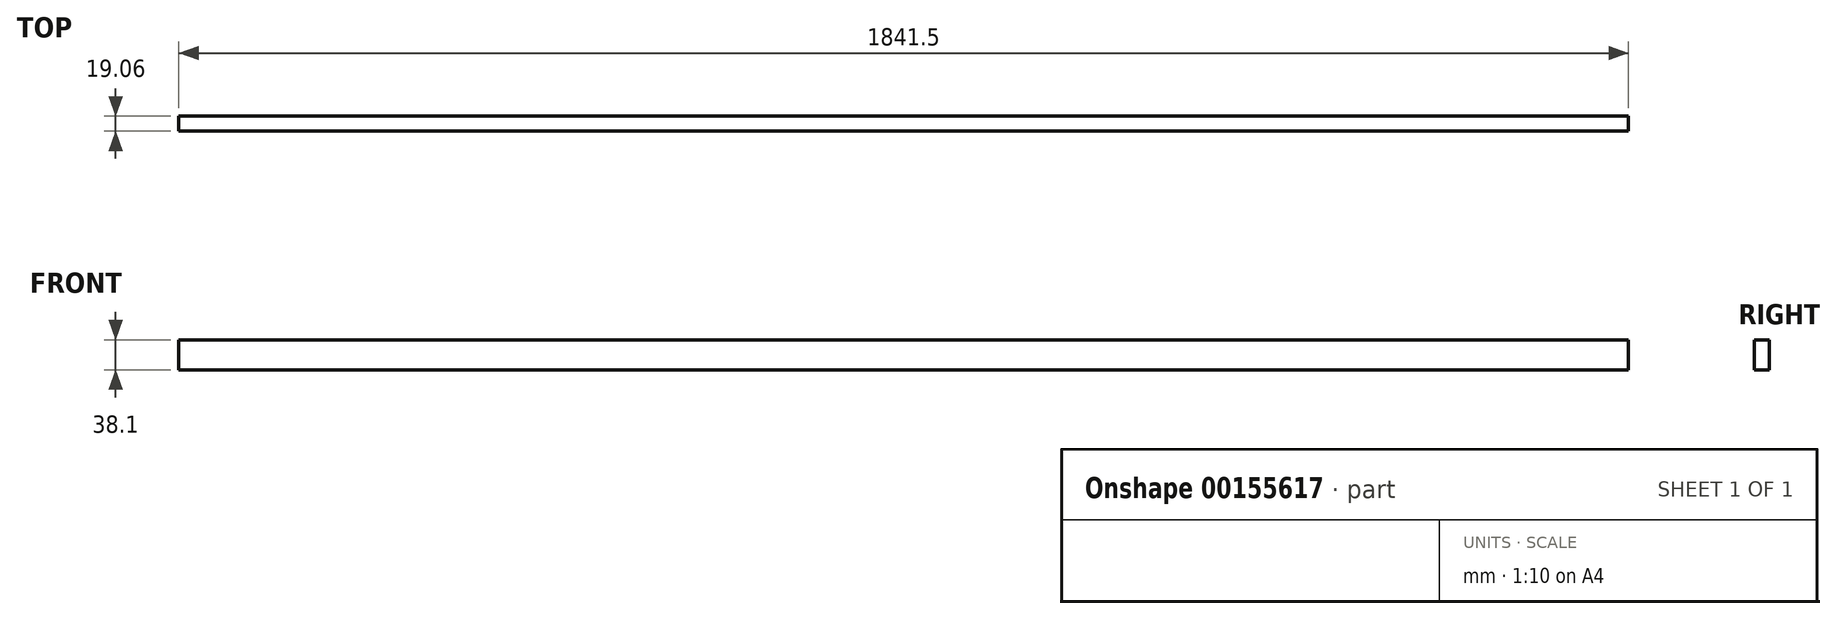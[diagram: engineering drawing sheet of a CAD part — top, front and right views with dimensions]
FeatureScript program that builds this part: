
annotation { "Feature Type Name" : "Feature", "Feature Type Description" : "" }
export const myFeature = defineFeature(function(context is Context, id is Id, definition is map)
    precondition{}
    {
        {
            var Q0;
            Q0=qCreatedBy(makeId("Right.planeOp"),FACE);
            var sketch = newSketch(context, id + "F0", { "sketchPlane" : qUnion([Q0])});
            skLineSegment(sketch, "E0.bottom", {"start": v(-9.52, 19.05) * mm, "end": v(9.53, 19.05) * mm});
            skLineSegment(sketch, "E0.top", {"start": v(-9.53, -19.05) * mm, "end": v(9.52, -19.05) * mm});
            skLineSegment(sketch, "E0.left", {"start": v(-9.52, 19.05) * mm, "end": v(-9.53, -19.05) * mm});
            skLineSegment(sketch, "E0.right", {"start": v(9.53, 19.05) * mm, "end": v(9.52, -19.05) * mm});
            skPoint(sketch, "E0.middle", {"position": v(0, 0) * mm});
            skSolve(sketch);
        }
        {
            var Q0;
            Q0 = qSketchRegion(id + "F0", true);
            extrude(context, id + "F1", {"entities" : qUnion([Q0]), "depth" : 1841.5 * mm});
        }
    });
